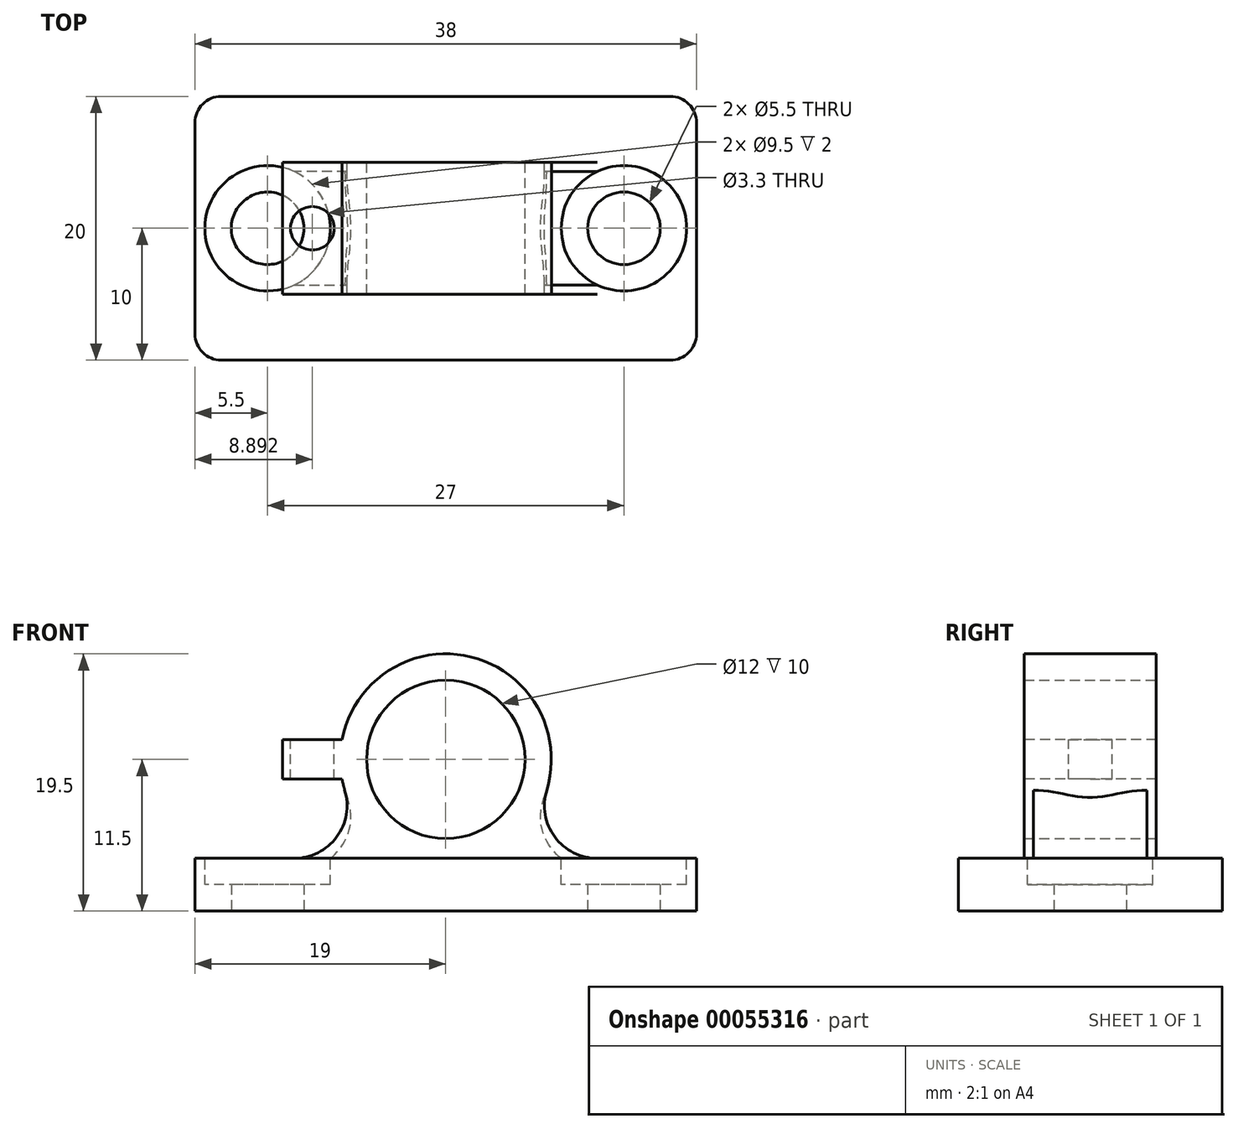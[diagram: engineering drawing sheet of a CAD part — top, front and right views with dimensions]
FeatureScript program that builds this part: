
annotation { "Feature Type Name" : "Feature", "Feature Type Description" : "" }
export const myFeature = defineFeature(function(context is Context, id is Id, definition is map)
    precondition{}
    {
        {
            var Q0;
            Q0=qCreatedBy(makeId("Front.planeOp"),FACE);
            var sketch = newSketch(context, id + "F0", { "sketchPlane" : qUnion([Q0])});
            skLineSegment(sketch, "E0", {"start": v(0, 0) * mm, "end": v(0, 30) * mm, "construction": true});
            skLineSegment(sketch, "E1.bottom", {"start": v(-19, 0) * mm, "end": v(19, 0) * mm});
            skLineSegment(sketch, "E1.top", {"start": v(-19, 4) * mm, "end": v(-2.78, 4) * mm});
            skLineSegment(sketch, "E1.left", {"start": v(-19, 0) * mm, "end": v(-19, 4) * mm});
            skLineSegment(sketch, "E1.right", {"start": v(19, 0) * mm, "end": v(19, 4) * mm});
            skCircle(sketch, "E2", {"center": v(0, 11.5) * mm, "radius": 6 * mm});
            skLineSegment(sketch, "E3", {"start": v(-2.78, 4) * mm, "end": v(2.78, 4) * mm, "construction": true});
            skLineSegment(sketch, "E4", {"start": v(2.78, 4) * mm, "end": v(19, 4) * mm});
            skArc(sketch, "E5", {"start": v(-2.78, 4) * mm, "mid": v(0, 3.5) * mm, "end": v(2.78, 4) * mm, "construction": true});
            skLineSegment(sketch, "E6", {"start": v(-2.78, 4) * mm, "end": v(-2.78, 4) * mm});
            skArc(sketch, "E7", {"start": v(2.78, 4) * mm, "mid": v(0, 19.5) * mm, "end": v(-2.78, 4) * mm});
            skSolve(sketch);
        }
        {
            var Q0;
            Q0=makeQuery(id+"F0.imprint","IMPRINT",FACE,{"disambiguationData":[TD([[makeQuery(id+"F0.imprint","IMPRINT",EDGE,{"derivedFrom":sQuery(id+"F0.wireOp",EDGE,"E1.bottom")}),1.0]])]});
            extrude(context, id + "F1", {"entities" : qUnion([Q0]), "depth" : 20 * mm});
        }
        {
            var Q0;
            Q0=makeQuery(id+"F1.opExtrude","CAP_FACE",FACE,{"disambiguationData":[OSD([sQuery(id+"F0.wireOp",EDGE,"E1.bottom"),sQuery(id+"F0.wireOp",EDGE,"E1.top"),sQuery(id+"F0.wireOp",EDGE,"E1.left"),sQuery(id+"F0.wireOp",EDGE,"E1.right"),sQuery(id+"F0.wireOp",EDGE,"E2"),sQuery(id+"F0.wireOp",EDGE,"E4"),sQuery(id+"F0.wireOp",EDGE,"E7")])],"isStart":false});
            var sketch = newSketch(context, id + "F2", { "sketchPlane" : qUnion([Q0])});
            skLineSegment(sketch, "E8", {"start": v(-2.78, 4) * mm, "end": v(2.78, 4) * mm});
            skSolve(sketch);
        }
        {
            var Q0;
            Q0=makeQuery(id+"F2.imprint","IMPRINT",FACE,{"disambiguationData":[TD([[makeQuery(id+"F2.imprint","IMPRINT",EDGE,{"derivedFrom":sQuery(id+"F2.wireOp",EDGE,"E8")}),1.0]])]});
            extrude(context, id + "F3", {"entities" : qUnion([Q0]), "operationType" : NewBodyOperationType.REMOVE, "oppositeDirection" : true, "depth" : 5 * mm});
        }
        {
            var Q0;
            Q0=makeQuery(id+"F1.opExtrude","CAP_FACE",FACE,{"disambiguationData":[OSD([sQuery(id+"F0.wireOp",EDGE,"E1.bottom"),sQuery(id+"F0.wireOp",EDGE,"E1.top"),sQuery(id+"F0.wireOp",EDGE,"E1.left"),sQuery(id+"F0.wireOp",EDGE,"E1.right"),sQuery(id+"F0.wireOp",EDGE,"E2"),sQuery(id+"F0.wireOp",EDGE,"E4"),sQuery(id+"F0.wireOp",EDGE,"E7")])],"isStart":true});
            var sketch = newSketch(context, id + "F4", { "sketchPlane" : qUnion([Q0])});
            skLineSegment(sketch, "E9", {"start": v(2.78, 4) * mm, "end": v(-2.78, 4) * mm});
            skSolve(sketch);
        }
        {
            var Q0;
            Q0=makeQuery(id+"F4.imprint","IMPRINT",FACE,{"disambiguationData":[TD([[makeQuery(id+"F4.imprint","IMPRINT",EDGE,{"derivedFrom":sQuery(id+"F4.wireOp",EDGE,"E9")}),-1.0]])]});
            extrude(context, id + "F5", {"entities" : qUnion([Q0]), "operationType" : NewBodyOperationType.REMOVE, "oppositeDirection" : true, "depth" : 5 * mm});
        }
        {
            var Q0;
            Q0=makeQuery(id+"F1.opExtrude","SWEPT_FACE",FACE,{"disambiguationData":[OSD([sQuery(id+"F0.wireOp",EDGE,"E1.bottom")])]});
            var sketch = newSketch(context, id + "F6", { "sketchPlane" : qUnion([Q0])});
            skLineSegment(sketch, "E10", {"start": v(-19, 10) * mm, "end": v(19, 10) * mm, "construction": true});
            skLineSegment(sketch, "E11", {"start": v(0, 20) * mm, "end": v(0, 0) * mm, "construction": true});
            skCircle(sketch, "E12", {"center": v(-13.5, 10) * mm, "radius": 2.75 * mm});
            skCircle(sketch, "E13", {"center": v(13.5, 10) * mm, "radius": 2.75 * mm});
            skSolve(sketch);
        }
        {
            var Q0;
            Q0=makeQuery(id+"F6.imprint","IMPRINT",FACE,{"disambiguationData":[TD([[makeQuery(id+"F6.imprint","IMPRINT",EDGE,{"derivedFrom":sQuery(id+"F6.wireOp",EDGE,"E12")}),1.0]])]});
            var Q1;
            Q1=makeQuery(id+"F6.imprint","IMPRINT",FACE,{"disambiguationData":[TD([[makeQuery(id+"F6.imprint","IMPRINT",EDGE,{"derivedFrom":sQuery(id+"F6.wireOp",EDGE,"E13")}),1.0]])]});
            extrude(context, id + "F7", {"entities" : qUnion([Q0, Q1]), "operationType" : NewBodyOperationType.REMOVE, "endBound" : BoundingType.THROUGH_ALL, "oppositeDirection" : true, "depth" : 25 * mm});
        }
        {
            var Q0;
            Q0=makeQuery(id+"F5.boolean.opBoolean","MERGE",FACE,{"derivedFrom":[makeQuery(id+"F3.boolean.opBoolean","MERGE",FACE,{"derivedFrom":[makeQuery(id+"F1.opExtrude","SWEPT_FACE",FACE,{"disambiguationData":[OSD([sQuery(id+"F0.wireOp",EDGE,"E1.top")])]}),makeQuery(id+"F1.opExtrude","SWEPT_FACE",FACE,{"disambiguationData":[OSD([sQuery(id+"F0.wireOp",EDGE,"E4")])]}),makeQuery(id+"F3.opExtrude","SWEPT_FACE",FACE,{"disambiguationData":[OSD([sQuery(id+"F2.wireOp",EDGE,"E8")])]})]}),makeQuery(id+"F5.opExtrude","SWEPT_FACE",FACE,{"disambiguationData":[OSD([sQuery(id+"F4.wireOp",EDGE,"E9")])]})]});
            var sketch = newSketch(context, id + "F8", { "sketchPlane" : qUnion([Q0])});
            skCircle(sketch, "E14", {"center": v(-13.5, -10) * mm, "radius": 4.75 * mm});
            skCircle(sketch, "E15", {"center": v(13.5, -10) * mm, "radius": 4.75 * mm});
            skSolve(sketch);
        }
        {
            var Q0;
            Q0=makeQuery(id+"F8.imprint","IMPRINT",FACE,{"disambiguationData":[TD([[makeQuery(id+"F8.imprint","IMPRINT",EDGE,{"derivedFrom":sQuery(id+"F8.wireOp",EDGE,"E14")}),1.0]])]});
            var Q1;
            Q1=makeQuery(id+"F8.imprint","IMPRINT",FACE,{"disambiguationData":[TD([[makeQuery(id+"F8.imprint","IMPRINT",EDGE,{"derivedFrom":sQuery(id+"F8.wireOp",EDGE,"E15")}),1.0]])]});
            extrude(context, id + "F9", {"entities" : qUnion([Q0, Q1]), "operationType" : NewBodyOperationType.REMOVE, "oppositeDirection" : true, "depth" : 2 * mm});
        }
        {
            var Q0;
            Q0=makeQuery(id+"F1.opExtrude","SWEPT_EDGE",EDGE,{"disambiguationData":[OSD([sQuery(id+"F0.wireOp",EDGE,"E1.top"),sQuery(id+"F0.wireOp",EDGE,"E7")])]});
            var Q1;
            Q1=makeQuery(id+"F1.opExtrude","SWEPT_EDGE",EDGE,{"disambiguationData":[OSD([sQuery(id+"F0.wireOp",EDGE,"E4"),sQuery(id+"F0.wireOp",EDGE,"E7")])]});
            fillet(context, id + "F10", {"entities" : qUnion([Q0, Q1]), "radius" : 4 * mm, "tangentPropagation" : true, "allowEdgeOverflow" : false});
        }
        {
            var Q0;
            Q0=makeQuery(id+"F1.opExtrude","CAP_EDGE",EDGE,{"disambiguationData":[OSD([sQuery(id+"F0.wireOp",EDGE,"E1.left")])],"isStart":true});
            var Q1;
            Q1=makeQuery(id+"F1.opExtrude","CAP_EDGE",EDGE,{"disambiguationData":[OSD([sQuery(id+"F0.wireOp",EDGE,"E1.left")])],"isStart":false});
            var Q2;
            Q2=makeQuery(id+"F1.opExtrude","CAP_EDGE",EDGE,{"disambiguationData":[OSD([sQuery(id+"F0.wireOp",EDGE,"E1.right")])],"isStart":false});
            var Q3;
            Q3=makeQuery(id+"F1.opExtrude","CAP_EDGE",EDGE,{"disambiguationData":[OSD([sQuery(id+"F0.wireOp",EDGE,"E1.right")])],"isStart":true});
            fillet(context, id + "F11", {"entities" : qUnion([Q0, Q1, Q2, Q3]), "radius" : 2 * mm, "tangentPropagation" : true, "allowEdgeOverflow" : false});
        }
        {
            var Q0;
            Q0=makeQuery(id+"F3.boolean.opBoolean","COPY",FACE,{"derivedFrom":makeQuery(id+"F3.opExtrude","CAP_FACE",FACE,{"disambiguationData":[OSD([sQuery(id+"F0.wireOp",EDGE,"E2"),sQuery(id+"F0.wireOp",EDGE,"E7"),sQuery(id+"F2.wireOp",EDGE,"E8")])],"isStart":false})});
            var sketch = newSketch(context, id + "F12", { "sketchPlane" : qUnion([Q0])});
            skLineSegment(sketch, "E16", {"start": v(-8.41, 11.5) * mm, "end": v(8.41, 11.5) * mm, "construction": true});
            skLineSegment(sketch, "E17", {"start": v(-12.36, 11.5) * mm, "end": v(-12.36, 13) * mm});
            skLineSegment(sketch, "E18", {"start": v(-12.36, 13) * mm, "end": v(-7.86, 13) * mm});
            skLineSegment(sketch, "E19", {"start": v(6, 11.5) * mm, "end": v(8, 11.5) * mm});
            skLineSegment(sketch, "E20", {"start": v(-12.36, 11.5) * mm, "end": v(-6, 11.5) * mm});
            skLineSegment(sketch, "E21", {"start": v(-12.36, 11.5) * mm, "end": v(-12.36, 10) * mm});
            skLineSegment(sketch, "E22", {"start": v(-12.36, 10) * mm, "end": v(-7.86, 10) * mm});
            skSolve(sketch);
        }
        {
            var Q0;
            {var subQ0=sQuery(id+"F12.wireOp",EDGE,"E17");Q0=makeQuery(id+"F12.imprint","IMPRINT",FACE,{"disambiguationData":[TD([[makeQuery(id+"F12.imprint","IMPRINT",EDGE,{"derivedFrom":subQ0}),-1.0]])]});}
            var Q1;
            {var subQ0=sQuery(id+"F12.wireOp",EDGE,"E21");Q1=makeQuery(id+"F12.imprint","IMPRINT",FACE,{"disambiguationData":[TD([[makeQuery(id+"F12.imprint","IMPRINT",EDGE,{"derivedFrom":subQ0}),1.0]])]});}
            var Q2;
            Q2=makeQuery(id+"F5.boolean.opBoolean","COPY",FACE,{"derivedFrom":makeQuery(id+"F5.opExtrude","CAP_FACE",FACE,{"disambiguationData":[OSD([sQuery(id+"F0.wireOp",EDGE,"E2"),sQuery(id+"F0.wireOp",EDGE,"E7"),sQuery(id+"F4.wireOp",EDGE,"E9")])],"isStart":false})});
            extrude(context, id + "F13", {"entities" : qUnion([Q0, Q1]), "operationType" : NewBodyOperationType.ADD, "endBound" : BoundingType.UP_TO_SURFACE, "oppositeDirection" : true, "endBoundEntityFace" : qUnion([Q2]), "depth" : 25 * mm});
        }
        {
            var Q0;
            Q0=makeQuery(id+"F13.opExtrude","SWEPT_FACE",FACE,{"disambiguationData":[OSD([sQuery(id+"F12.wireOp",EDGE,"E18")])]});
            var sketch = newSketch(context, id + "F14", { "sketchPlane" : qUnion([Q0])});
            skCircle(sketch, "E23", {"center": v(-10.1, -10) * mm, "radius": 1.65 * mm});
            skPoint(sketch, "E23.centerSnap0", {"position": v(-12.36, -10) * mm});
            skPoint(sketch, "E23.centerSnap1", {"position": v(-10.1, -5) * mm});
            skSolve(sketch);
        }
        {
            var Q0;
            Q0=makeQuery(id+"F14.imprint","IMPRINT",FACE,{"disambiguationData":[TD([[makeQuery(id+"F14.imprint","IMPRINT",EDGE,{"derivedFrom":sQuery(id+"F14.wireOp",EDGE,"E23")}),1.0]])]});
            var Q1;
            Q1=makeQuery(id+"F13.opExtrude","SWEPT_FACE",FACE,{"disambiguationData":[OSD([sQuery(id+"F12.wireOp",EDGE,"E22")])]});
            extrude(context, id + "F15", {"entities" : qUnion([Q0]), "operationType" : NewBodyOperationType.REMOVE, "endBound" : BoundingType.UP_TO_SURFACE, "oppositeDirection" : true, "endBoundEntityFace" : qUnion([Q1]), "depth" : 25 * mm});
        }
    });
